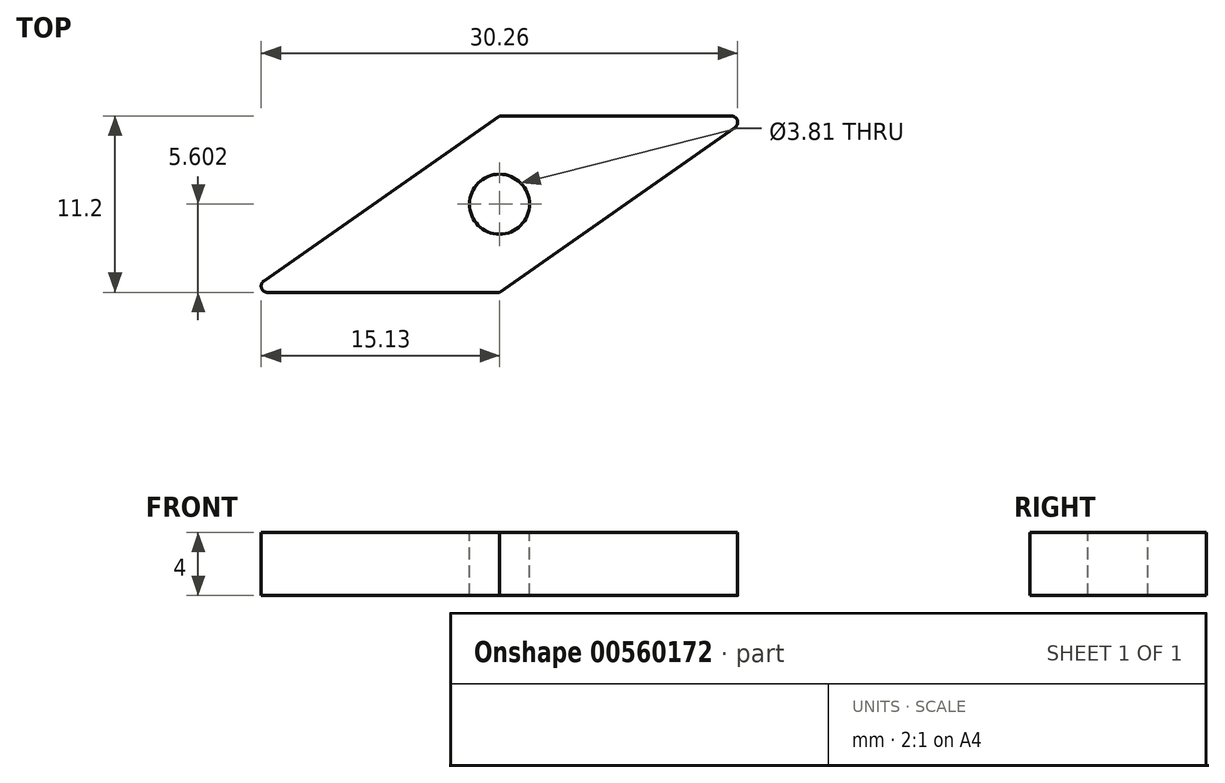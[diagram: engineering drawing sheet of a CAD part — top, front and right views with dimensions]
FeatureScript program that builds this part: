
annotation { "Feature Type Name" : "Feature", "Feature Type Description" : "" }
export const myFeature = defineFeature(function(context is Context, id is Id, definition is map)
    precondition{}
    {
        {
            var Q0;
            Q0=qCreatedBy(makeId("Top.planeOp"),FACE);
            var sketch = newSketch(context, id + "F0", { "sketchPlane" : qUnion([Q0])});
            skLineSegment(sketch, "E0", {"start": v(0, 0) * mm, "end": v(-16, 0) * mm});
            skLineSegment(sketch, "E1", {"start": v(-16, 0) * mm, "end": v(0, 11.2) * mm});
            skLineSegment(sketch, "E2", {"start": v(0, 11.2) * mm, "end": v(16, 11.2) * mm});
            skLineSegment(sketch, "E3", {"start": v(16, 11.2) * mm, "end": v(0, 0) * mm});
            skSolve(sketch);
        }
        {
            var Q0;
            Q0 = qSketchRegion(id + "F0", true);
            extrude(context, id + "F1", {"entities" : qUnion([Q0]), "depth" : 4 * mm, "offsetDistance" : 25 * mm});
        }
        {
            var Q0;
            Q0=makeQuery(id+"F1.opExtrude","SWEPT_EDGE",EDGE,{"disambiguationData":[OSD([sQuery(id+"F0.wireOp",EDGE,"E0"),sQuery(id+"F0.wireOp",EDGE,"E1")])]});
            var Q1;
            Q1=makeQuery(id+"F1.opExtrude","SWEPT_EDGE",EDGE,{"disambiguationData":[OSD([sQuery(id+"F0.wireOp",EDGE,"E2"),sQuery(id+"F0.wireOp",EDGE,"E3")])]});
            fillet(context, id + "F2", {"entities" : qUnion([Q0, Q1]), "radius" : 0.4 * mm, "tangentPropagation" : true, "allowEdgeOverflow" : false});
        }
        {
            var Q0;
            Q0=makeQuery(id+"F1.opExtrude","CAP_FACE",FACE,{"disambiguationData":[OSD([sQuery(id+"F0.wireOp",EDGE,"E0"),sQuery(id+"F0.wireOp",EDGE,"E1"),sQuery(id+"F0.wireOp",EDGE,"E2"),sQuery(id+"F0.wireOp",EDGE,"E3")])],"isStart":false});
            var sketch = newSketch(context, id + "F3", { "sketchPlane" : qUnion([Q0])});
            skLineSegment(sketch, "E4", {"start": v(0, 11.2) * mm, "end": v(0, 0) * mm, "construction": true});
            skPoint(sketch, "E5", {"position": v(0, 5.6) * mm});
            skCircle(sketch, "E6", {"center": v(0, 5.6) * mm, "radius": 1.9 * mm});
            skSolve(sketch);
        }
        {
            var Q0;
            Q0 = qSketchRegion(id + "F3", true);
            extrude(context, id + "F4", {"entities" : qUnion([Q0]), "operationType" : NewBodyOperationType.REMOVE, "endBound" : BoundingType.UP_TO_NEXT, "oppositeDirection" : true, "depth" : 25 * mm, "offsetDistance" : 25 * mm});
        }
    });
